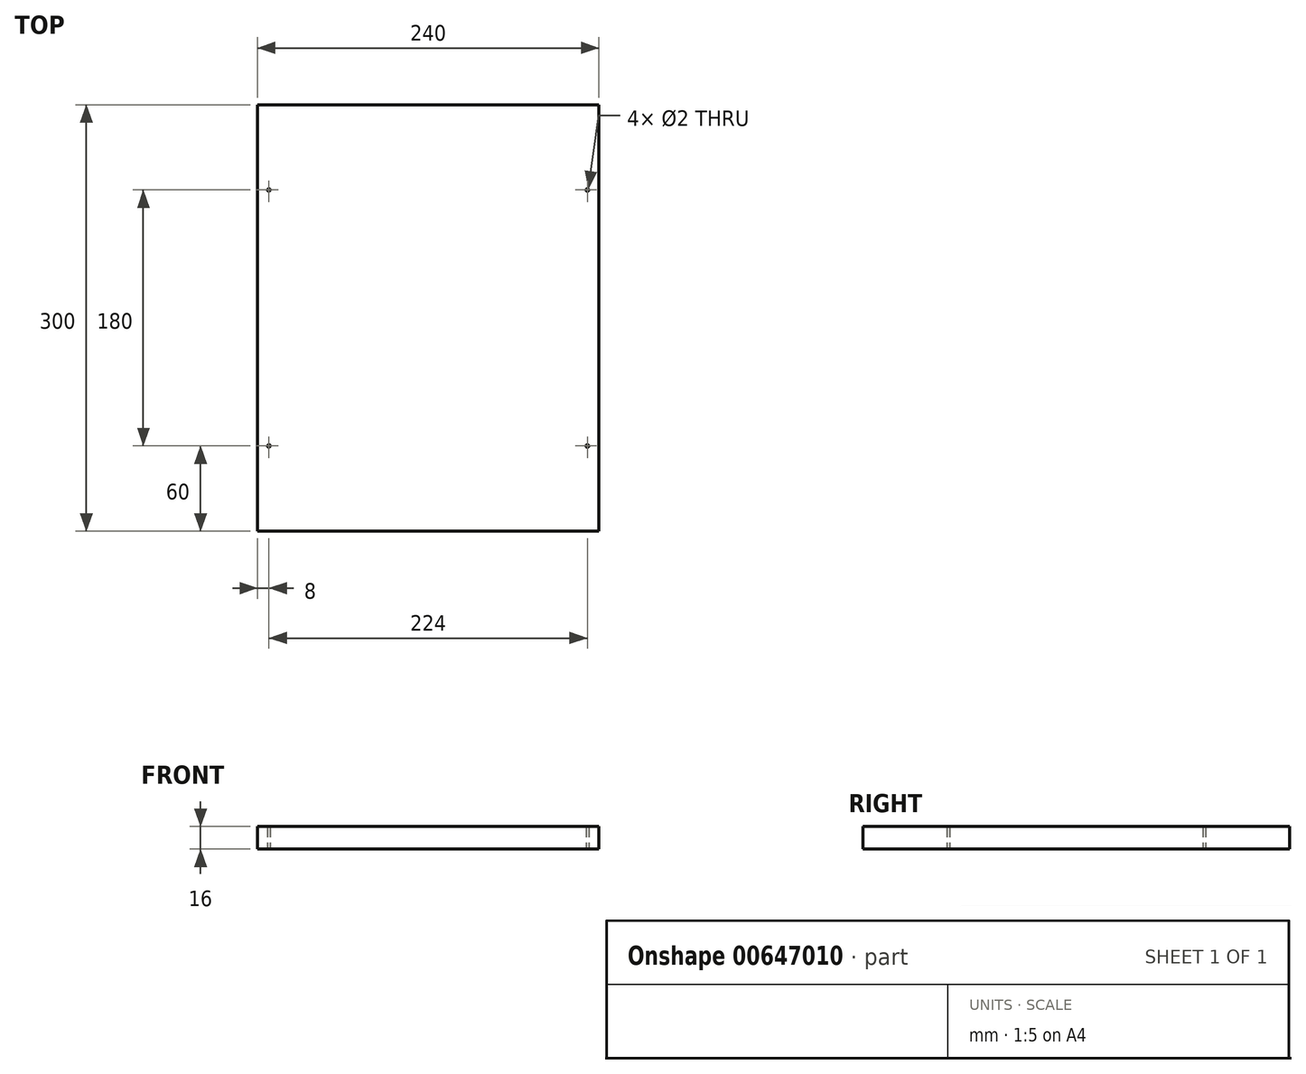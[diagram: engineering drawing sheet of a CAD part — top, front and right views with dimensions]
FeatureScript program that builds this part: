
annotation { "Feature Type Name" : "Feature", "Feature Type Description" : "" }
export const myFeature = defineFeature(function(context is Context, id is Id, definition is map)
    precondition{}
    {
        {
            var Q0;
            Q0=qCreatedBy(makeId("Top.planeOp"),FACE);
            var sketch = newSketch(context, id + "F0", { "sketchPlane" : qUnion([Q0])});
            skLineSegment(sketch, "E0.bottom", {"start": v(120, -150) * mm, "end": v(-120, -150) * mm});
            skLineSegment(sketch, "E0.top", {"start": v(120, 150) * mm, "end": v(-120, 150) * mm});
            skLineSegment(sketch, "E0.left", {"start": v(120, -150) * mm, "end": v(120, 150) * mm});
            skLineSegment(sketch, "E0.right", {"start": v(-120, -150) * mm, "end": v(-120, 150) * mm});
            skPoint(sketch, "E0.middle", {"position": v(0, 0) * mm});
            skLineSegment(sketch, "E1", {"start": v(-112, 90) * mm, "end": v(-112, -90) * mm, "construction": true});
            skCircle(sketch, "E2", {"center": v(-112, 90) * mm, "radius": 1 * mm});
            skCircle(sketch, "E3", {"center": v(-112, -90) * mm, "radius": 1 * mm});
            skCircle(sketch, "E4.MirrorC", {"center": v(112, -90) * mm, "radius": 1 * mm});
            skCircle(sketch, "E5.MirrorC", {"center": v(112, 90) * mm, "radius": 1 * mm});
            skSolve(sketch);
        }
        {
            var Q0;
            Q0=makeQuery(id+"F0.imprint","IMPRINT",FACE,{"disambiguationData":[TD([[makeQuery(id+"F0.imprint","IMPRINT",EDGE,{"derivedFrom":sQuery(id+"F0.wireOp",EDGE,"E0.bottom")}),-1.0]])]});
            extrude(context, id + "F1", {"entities" : qUnion([Q0]), "depth" : 16 * mm, "offsetDistance" : 25 * mm});
        }
    });
